# Revit family: CPVC
name_source: partatom
category: Pipe Accessories
units: mm (PartAtom-declared; Revit-internal decimal feet)

## family parameters
Always vertical = Yes
Cut with Voids When Loaded = No
Part Type = Valve - Breaks Into
Round Connector Dimension = Use Diameter
Shared = No
Work Plane-Based = No

## types (3) — shared parameters
D1 = 4 mm  [stored 0.0131234 ft]
Description = VÁLVULAS DE BOLA COMPACTAS EN CPVC PARA USO CON AGUA CALIENTE
Imagen = https://pcpplasticos.co
Manufacturer = PCP PLASTICOS
URL = https://pcpplasticos.co
zero-valued in all types: Default Elevation

## per-type parameters (varying)
| type | 1" | 1/2" | 3/4" | D | Model | SKU | d1 | d2 |
| Diametro 1/2" | No | Yes | No | 13 mm | 3748 | 3748 | 30 mm  [stored 0.0984252 ft] | 29 mm |
| Diametro 3/4" | No | No | Yes | 19 mm | 3749 | 3749 | 40 mm  [stored 0.131234 ft] | 39 mm |
| Diametro 1" | Yes | No | No | 25 mm  [stored 0.082021 ft] | 3747 | 3747 | 46 mm  [stored 0.150919 ft] | 45 mm |

note: [stored X ft] marks values corroborated as IEEE doubles in the binary element streams (Revit-internal decimal feet)

## geometry (parser evidence)
native form markers: Sweep x2
no freeform markers — native parametric forms only
